# Revit family: Gira_049544
name_source: partatom
category: Elektroinstallationen
revit_build: Autodesk Revit 2017 (Build: 20160225_1515(x64)
units: mm (PartAtom-declared; Revit-internal decimal feet)

## family parameters
Basisbauteil = Wand
Beim Laden mit Abzugskörper schneiden = Nein
Bemaßung runder Anschluss = Durchmesser verwenden
Beschriftungsausrichtung beibehalten = Nein
Gemeinsam genutzt = Nein
Immer vertikal = Ja
OmniClass-Nummer = 23.80.00.00
OmniClass-Titel = Electric Power and Lighting
Raumberechnungspunkt = Nein
Teiletyp = Normal

## types (1)
- Gira_049544
    Anzahl der Außenstationen = 1
    Anzahl der Innenstationen = 2
    BIM = https://media.stage.bim.site Audio.rfa
    Beschreibung = Zweifamilienhaus-Paket Audio
    Datenblatt = https://katalog.gira.de
    Farbe der Außenstation = sonstige
    Farbe der Innenstation = weiß
    GTIN = 4010337495444
    HAN = 049544
    Hersteller = Gira
    Installationstechnik = Bus-System
    Mit Infoschild = Ja
    Mit Video = Nein
    Produktseite = http://katalog.gira.de
    Typname = ZFH-Paket Audio Türko F Alu
    URL = https://www.gira.de

## geometry (parser evidence)
native form markers: Sweep x7
no freeform markers — native parametric forms only
